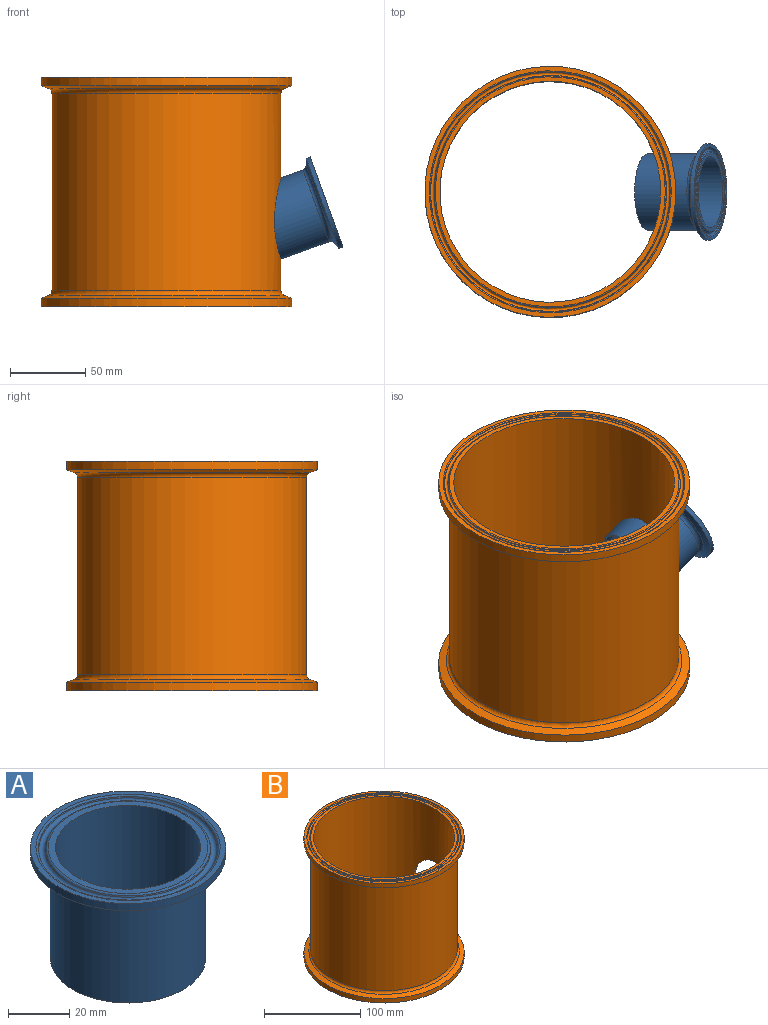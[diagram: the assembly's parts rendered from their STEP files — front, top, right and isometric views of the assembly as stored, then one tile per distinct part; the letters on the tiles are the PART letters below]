
ASSEMBLY  parts=2 mates=1
PART A: 13 faces, bbox 65.3x65.3x44.5 mm
  f0: plane 63.91x63.91mm, normal (0,0,1), area 350.1mm2, adj f1,f11
  f1: torus R=30.16mm, axis (0,0,1), area 172.1mm2, adj f0,f2
  f2: cone r=29.43mm half-angle=23deg, axis (0,0,1), area 78.8mm2, adj f1,f3
  f3: torus R=28.17mm, axis (0,0,1), area 494.2mm2, adj f2,f4
  f4: cone r=27.07mm half-angle=23deg, axis (0,0,-1), area 72.4mm2, adj f3,f5
  f5: torus R=26.18mm, axis (0,0,1), area 153.8mm2, adj f4,f6
  f6: plane 52.36x52.36mm, normal (0,0,1), area 381mm2, adj f5,f7
  f7: cylinder r=23.75mm len=47.5mm, axis (0,0,1), area 6632.8mm2, adj f6,f12
  f8: cylinder r=25.4mm len=50.8mm, axis (0,0,1), area 5904.4mm2, adj f9,f12
  f9: torus R=28.57mm, axis (0,0,1), area 636.9mm2, adj f8,f10
  f10: cone r=27.49mm half-angle=70deg, axis (0,0,1), area 887.1mm2, adj f9,f11
  f11: cylinder r=31.95mm len=63.91mm, axis (0,0,1), area 571.1mm2, adj f0,f10
  f12: plane 50.8x50.8mm, normal (0,0,-1), area 254.9mm2, adj f7,f8
PART B: 23 faces, bbox 181.2x175.3x152.4 mm
  f0: plane 166.88x166.88mm, normal (0,0,1), area 1551.2mm2, adj f1,f21
  f1: torus R=80.43mm, axis (0,0,1), area 462.9mm2, adj f0,f2
  f2: cone r=79.7mm half-angle=23deg, axis (0,0,1), area 213.6mm2, adj f1,f3
  f3: torus R=78.44mm, axis (0,0,1), area 1376mm2, adj f2,f4
  f4: cone r=77.34mm half-angle=23deg, axis (0,0,-1), area 207.3mm2, adj f3,f5
  f5: torus R=76.44mm, axis (0,0,1), area 444.6mm2, adj f4,f6
  f6: plane 152.89x152.89mm, normal (0,0,1), area 1418.8mm2, adj f5,f7
  f7: cylinder r=73.43mm len=152.4mm, axis (0,0,1), area 68122.6mm2, adj f6,f8,f22
  f8: plane 152.89x152.89mm, normal (0,0,-1), area 1418.8mm2, adj f7,f9
  f9: torus R=76.44mm, axis (0,0,1), area 444.6mm2, adj f8,f10
  f10: cone r=77.17mm half-angle=23deg, axis (0,0,1), area 207.3mm2, adj f9,f11
  f11: torus R=78.44mm, axis (0,0,1), area 1376mm2, adj f10,f12
  f12: cone r=79.53mm half-angle=23deg, axis (0,0,-1), area 213.6mm2, adj f11,f13
  f13: torus R=80.43mm, axis (0,0,1), area 462.9mm2, adj f12,f14
  f14: plane 166.88x166.88mm, normal (0,0,-1), area 1551.2mm2, adj f13,f15
  f15: cylinder r=83.44mm len=166.88mm, axis (0,0,1), area 2929.6mm2, adj f14,f16
  f16: cone r=83.44mm half-angle=70deg, axis (0,0,-1), area 2784.5mm2, adj f15,f17
  f17: torus R=79.38mm, axis (0,0,1), area 1875mm2, adj f16,f18
  f18: cylinder r=76.2mm len=152.4mm, axis (0,0,1), area 60771.6mm2, adj f17,f19,f22
  f19: torus R=79.38mm, axis (0,0,1), area 1875mm2, adj f18,f20
  f20: cone r=78.29mm half-angle=70deg, axis (0,0,1), area 2784.5mm2, adj f19,f21
  f21: cylinder r=83.44mm len=166.88mm, axis (0,0,1), area 2929.6mm2, adj f0,f20
  f22: cylinder r=25.4mm len=55.07mm, axis (-0.94,0,-0.34), area 485.1mm2, adj f7,f18
PLACE A rot(axis=(0,1,0),70deg) t=(120.85,-34.93,-68.01)mm
PLACE B t=(14.33,-34.93,14.85)mm fixed
MATE cylindrical A.f1 <-> B.f22  axis (0.94,0,0.34) through (79.08,-34.93,-83.22)mm
